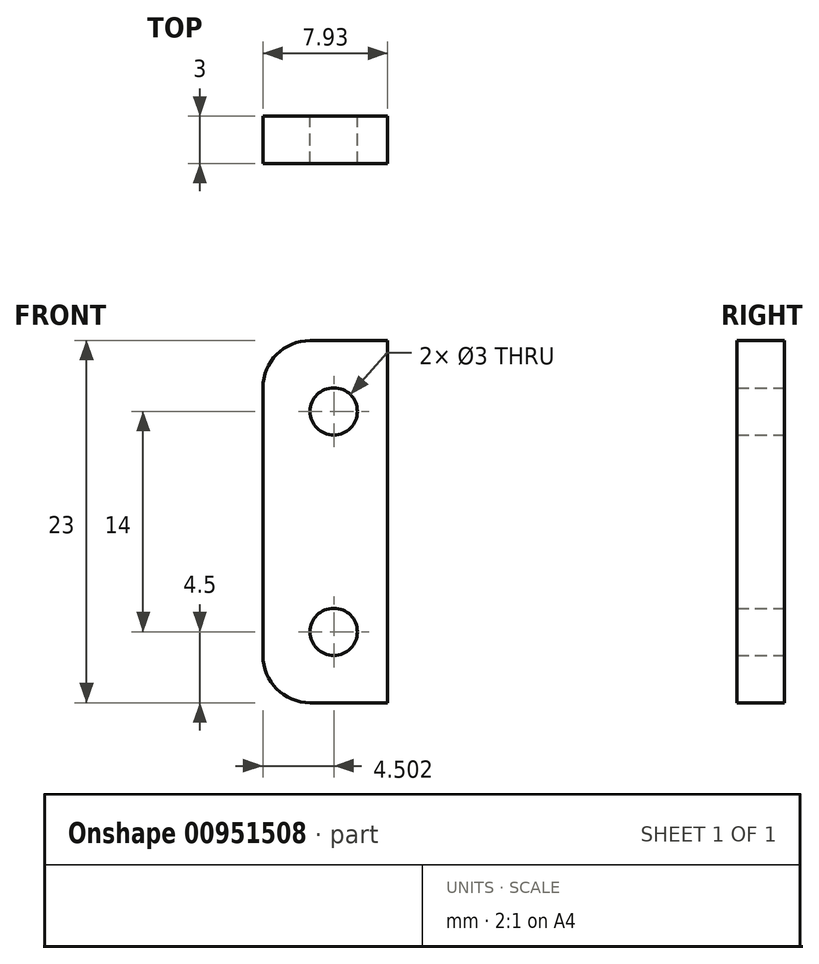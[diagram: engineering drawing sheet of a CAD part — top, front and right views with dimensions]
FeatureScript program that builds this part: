
annotation { "Feature Type Name" : "Feature", "Feature Type Description" : "" }
export const myFeature = defineFeature(function(context is Context, id is Id, definition is map)
    precondition{}
    {
        {
            var Q0;
            Q0=qCreatedBy(makeId("Front.planeOp"),FACE);
            var sketch = newSketch(context, id + "F0", { "sketchPlane" : qUnion([Q0])});
            skLineSegment(sketch, "E0.bottom", {"start": v(-8.43, -11.5) * mm, "end": v(8.43, -11.5) * mm});
            skLineSegment(sketch, "E0.top", {"start": v(-8.43, 11.5) * mm, "end": v(8.43, 11.5) * mm});
            skLineSegment(sketch, "E0.left", {"start": v(-11.43, -8.5) * mm, "end": v(-11.43, 8.5) * mm});
            skLineSegment(sketch, "E0.right", {"start": v(11.43, -8.5) * mm, "end": v(11.43, 8.5) * mm});
            skCircle(sketch, "E1", {"center": v(0, 6) * mm, "radius": 2.5 * mm});
            skCircle(sketch, "E2", {"center": v(0, -6) * mm, "radius": 2.5 * mm});
            skCircle(sketch, "E3", {"center": v(6.93, 7) * mm, "radius": 1.5 * mm});
            skCircle(sketch, "E4", {"center": v(-6.93, 7) * mm, "radius": 1.5 * mm});
            skCircle(sketch, "E5", {"center": v(-6.93, -7) * mm, "radius": 1.5 * mm});
            skCircle(sketch, "E6", {"center": v(6.93, -7) * mm, "radius": 1.5 * mm});
            skPoint(sketch, "E7.visualSharp", {"position": v(11.43, 11.5) * mm});
            skArc(sketch, "E7.filletArc", {"start": v(11.43, 8.5) * mm, "mid": v(10.55, 10.62) * mm, "end": v(8.43, 11.5) * mm});
            skPoint(sketch, "E8.visualSharp", {"position": v(-11.43, 11.5) * mm});
            skArc(sketch, "E8.filletArc", {"start": v(-8.43, 11.5) * mm, "mid": v(-10.55, 10.62) * mm, "end": v(-11.43, 8.5) * mm});
            skPoint(sketch, "E9.visualSharp", {"position": v(-11.43, -11.5) * mm});
            skArc(sketch, "E9.filletArc", {"start": v(-11.43, -8.5) * mm, "mid": v(-10.55, -10.62) * mm, "end": v(-8.43, -11.5) * mm});
            skPoint(sketch, "E10.visualSharp", {"position": v(11.43, -11.5) * mm});
            skArc(sketch, "E10.filletArc", {"start": v(8.43, -11.5) * mm, "mid": v(10.55, -10.62) * mm, "end": v(11.43, -8.5) * mm});
            skLineSegment(sketch, "E11", {"start": v(3.5, 11.5) * mm, "end": v(3.5, -11.5) * mm});
            skLineSegment(sketch, "E12", {"start": v(-3.5, 11.5) * mm, "end": v(-3.5, -11.5) * mm});
            skSolve(sketch);
        }
        {
            var Q0;
            Q0=makeQuery(id+"F0.imprint","IMPRINT",FACE,{"disambiguationData":[TD([[makeQuery(id+"F0.imprint","IMPRINT",EDGE,{"derivedFrom":sQuery(id+"F0.wireOp",EDGE,"E0.left")}),-1.0]])]});
            extrude(context, id + "F1", {"entities" : qUnion([Q0]), "depth" : 3 * mm, "offsetDistance" : 25 * mm});
        }
    });
